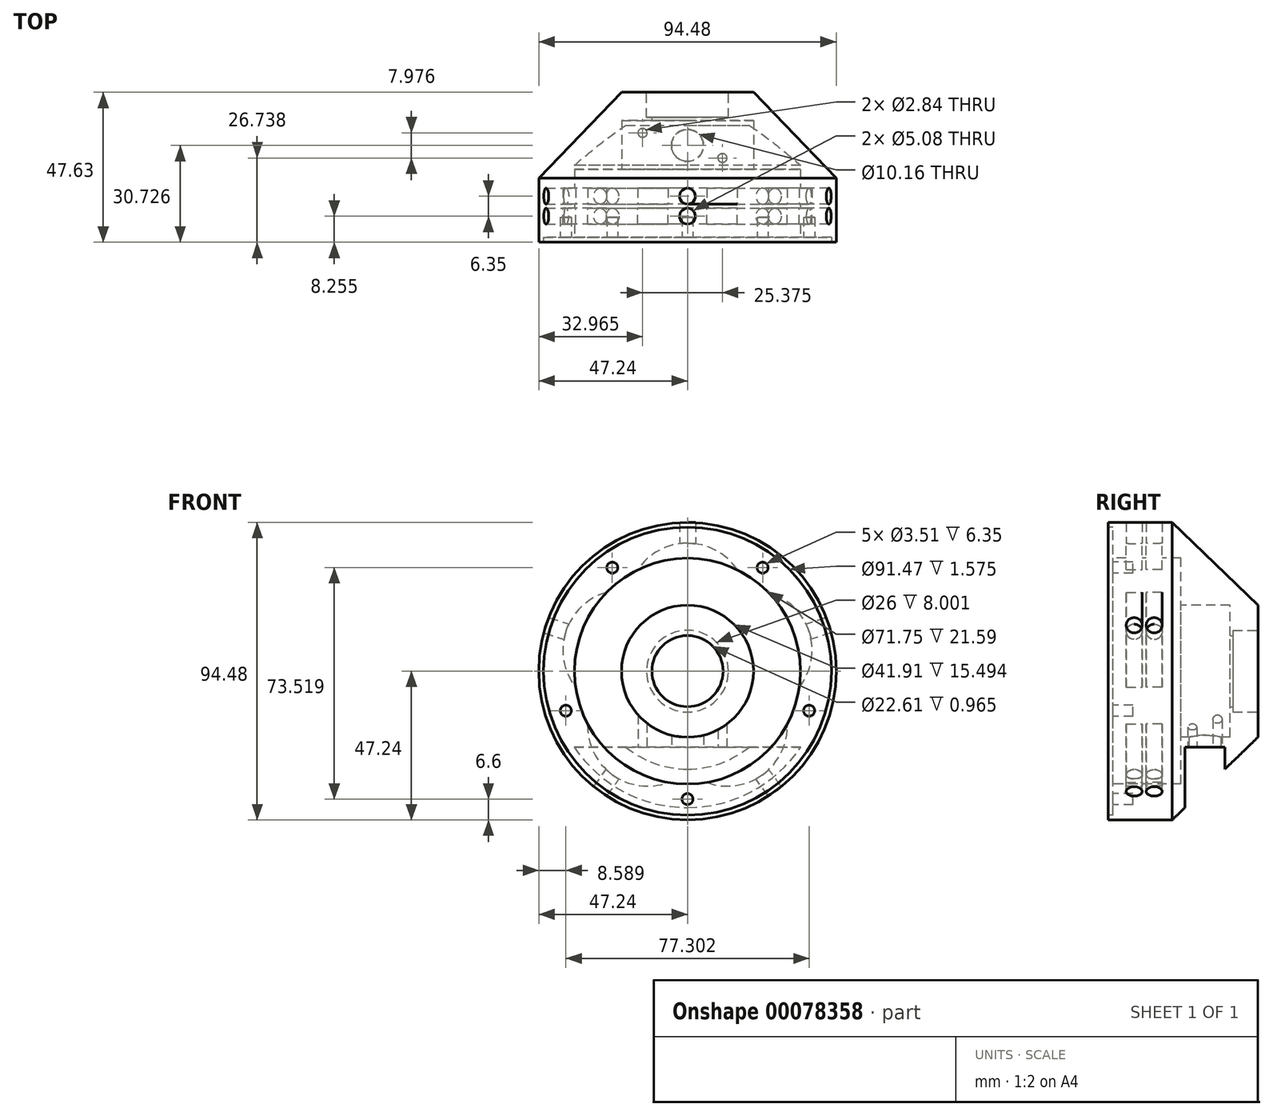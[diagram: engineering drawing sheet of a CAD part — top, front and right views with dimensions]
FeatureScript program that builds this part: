
annotation { "Feature Type Name" : "Feature", "Feature Type Description" : "" }
export const myFeature = defineFeature(function(context is Context, id is Id, definition is map)
    precondition{}
    {
        {
            var Q0;
            Q0=qCreatedBy(makeId("Front.planeOp"),FACE);
            var sketch = newSketch(context, id + "F0", { "sketchPlane" : qUnion([Q0])});
            skCircle(sketch, "E0", {"center": v(0, 0) * mm, "radius": 47.24 * mm});
            skSolve(sketch);
        }
        {
            var Q0;
            Q0 = qSketchRegion(id + "F0", true);
            extrude(context, id + "F1", {"entities" : qUnion([Q0]), "depth" : 20.32 * mm});
        }
        {
            var Q0;
            Q0=makeQuery(id+"F1.opExtrude","CAP_FACE",FACE,{"disambiguationData":[OSD([sQuery(id+"F0.wireOp",EDGE,"E0")])],"isStart":false});
            var sketch = newSketch(context, id + "F2", { "sketchPlane" : qUnion([Q0])});
            skCircle(sketch, "E1", {"center": v(0, 0) * mm, "radius": 45.73 * mm});
            skSolve(sketch);
        }
        {
            var Q0;
            Q0 = qSketchRegion(id + "F2", true);
            extrude(context, id + "F3", {"entities" : qUnion([Q0]), "operationType" : NewBodyOperationType.REMOVE, "oppositeDirection" : true, "depth" : 1.57 * mm});
        }
        {
            var Q0;
            Q0=qCreatedBy(makeId("Right.planeOp"),FACE);
            var sketch = newSketch(context, id + "F4", { "sketchPlane" : qUnion([Q0])});
            skLineSegment(sketch, "E2", {"start": v(0, 0) * mm, "end": v(27.3, 0) * mm});
            skLineSegment(sketch, "E3", {"start": v(27.3, 0) * mm, "end": v(27.3, 20.96) * mm});
            skLineSegment(sketch, "E4", {"start": v(0, 0) * mm, "end": v(0, 47.24) * mm});
            skLineSegment(sketch, "E5", {"start": v(0, 47.24) * mm, "end": v(27.3, 20.96) * mm});
            skSolve(sketch);
        }
        {
            var Q0;
            Q0 = qSketchRegion(id + "F4", true);
            var Q1;
            Q1=sQuery(id+"F4.wireOp",EDGE,"E2");
            revolve(context, id + "F5", {"operationType" : NewBodyOperationType.ADD, "entities" : qUnion([Q0]), "axis" : qUnion([Q1]), "revolveType" : RevolveType.FULL});
        }
        {
            var Q0;
            Q0=makeQuery(id+"F5.opRevolve","SWEPT_FACE",FACE,{"disambiguationData":[OSD([sQuery(id+"F4.wireOp",EDGE,"E3")])]});
            var sketch = newSketch(context, id + "F6", { "sketchPlane" : qUnion([Q0])});
            skCircle(sketch, "E6", {"center": v(0, 0) * mm, "radius": 13 * mm});
            skSolve(sketch);
        }
        {
            var Q0;
            Q0 = qSketchRegion(id + "F6", true);
            extrude(context, id + "F7", {"entities" : qUnion([Q0]), "operationType" : NewBodyOperationType.REMOVE, "oppositeDirection" : true, "depth" : 8 * mm});
        }
        {
            var Q0;
            Q0=makeQuery(id+"F3.boolean.opBoolean","COPY",FACE,{"derivedFrom":makeQuery(id+"F3.opExtrude","CAP_FACE",FACE,{"disambiguationData":[OSD([sQuery(id+"F2.wireOp",EDGE,"E1")])],"isStart":false})});
            var sketch = newSketch(context, id + "F8", { "sketchPlane" : qUnion([Q0])});
            skCircle(sketch, "E7", {"center": v(0, 0) * mm, "radius": 35.88 * mm});
            skSolve(sketch);
        }
        {
            var Q0;
            Q0 = qSketchRegion(id + "F8", true);
            extrude(context, id + "F9", {"entities" : qUnion([Q0]), "operationType" : NewBodyOperationType.REMOVE, "oppositeDirection" : true, "depth" : 21.59 * mm});
        }
        {
            var Q0;
            Q0=makeQuery(id+"F9.boolean.opBoolean","COPY",FACE,{"derivedFrom":makeQuery(id+"F9.opExtrude","CAP_FACE",FACE,{"disambiguationData":[OSD([sQuery(id+"F8.wireOp",EDGE,"E7")])],"isStart":false})});
            var sketch = newSketch(context, id + "F10", { "sketchPlane" : qUnion([Q0])});
            skCircle(sketch, "E8", {"center": v(0, 0) * mm, "radius": 20.96 * mm});
            skSolve(sketch);
        }
        {
            var Q0;
            Q0 = qSketchRegion(id + "F10", true);
            extrude(context, id + "F11", {"entities" : qUnion([Q0]), "operationType" : NewBodyOperationType.REMOVE, "oppositeDirection" : true, "depth" : 15.5 * mm});
        }
        {
            var Q0;
            Q0=makeQuery(id+"F7.boolean.opBoolean","COPY",FACE,{"derivedFrom":makeQuery(id+"F7.opExtrude","CAP_FACE",FACE,{"disambiguationData":[OSD([sQuery(id+"F6.wireOp",EDGE,"E6")])],"isStart":false})});
            var sketch = newSketch(context, id + "F12", { "sketchPlane" : qUnion([Q0])});
            skCircle(sketch, "E9", {"center": v(0, 0) * mm, "radius": 11.3 * mm});
            skSolve(sketch);
        }
        {
            var Q0;
            Q0 = qSketchRegion(id + "F12", true);
            extrude(context, id + "F13", {"entities" : qUnion([Q0]), "operationType" : NewBodyOperationType.REMOVE, "oppositeDirection" : true, "depth" : 25.4 * mm});
        }
        {
            var Q0;
            Q0=qCreatedBy(makeId("Top.planeOp"),FACE);
            cPlane(context, id + "F14", {"entities" : qUnion([Q0]), "cplaneType" : CPlaneType.OFFSET, "offset" : 24.13 * mm, "oppositeDirection" : true, "width" : 152.4 * mm, "height" : 152.4 * mm});
        }
        {
            var Q0;
            Q0=qCreatedBy(id+"F14.planeOp",FACE);
            var sketch = newSketch(context, id + "F15", { "sketchPlane" : qUnion([Q0])});
            skLineSegment(sketch, "E10", {"start": v(0, 16.76) * mm, "end": v(-59.54, 16.76) * mm});
            skLineSegment(sketch, "E11", {"start": v(0, 4.06) * mm, "end": v(-59.54, 4.06) * mm});
            skLineSegment(sketch, "E12", {"start": v(-59.54, 4.06) * mm, "end": v(-59.54, 16.76) * mm});
            skLineSegment(sketch, "E13.MirrorCS", {"start": v(0, 4.06) * mm, "end": v(59.54, 4.06) * mm});
            skLineSegment(sketch, "E14.MirrorCS", {"start": v(0, 16.76) * mm, "end": v(59.54, 16.76) * mm});
            skLineSegment(sketch, "E15.MirrorCS", {"start": v(59.54, 4.06) * mm, "end": v(59.54, 16.76) * mm});
            skSolve(sketch);
        }
        {
            var Q0;
            Q0 = qSketchRegion(id + "F15", true);
            extrude(context, id + "F16", {"entities" : qUnion([Q0]), "operationType" : NewBodyOperationType.REMOVE, "oppositeDirection" : true, "depth" : 25.4 * mm});
        }
        {
            var Q0;
            Q0=makeQuery(id+"F16.boolean.opBoolean","COPY",FACE,{"derivedFrom":makeQuery(id+"F16.opExtrude","CAP_FACE",FACE,{"disambiguationData":[OSD([sQuery(id+"F15.wireOp",EDGE,"E10"),sQuery(id+"F15.wireOp",EDGE,"E11"),sQuery(id+"F15.wireOp",EDGE,"E12"),sQuery(id+"F15.wireOp",EDGE,"E13.MirrorCS"),sQuery(id+"F15.wireOp",EDGE,"E14.MirrorCS"),sQuery(id+"F15.wireOp",EDGE,"E15.MirrorCS")])],"isStart":true})});
            var sketch = newSketch(context, id + "F17", { "sketchPlane" : qUnion([Q0])});
            skPoint(sketch, "E16.endSnap0", {"position": v(0, -16.76) * mm});
            skCircle(sketch, "E17", {"center": v(0, -10.4) * mm, "radius": 5.08 * mm});
            skLineSegment(sketch, "E18", {"start": v(0, -10.4) * mm, "end": v(11.1, -10.4) * mm, "construction": true});
            skLineSegment(sketch, "E19", {"start": v(0, -10.4) * mm, "end": v(-14.27, -10.4) * mm, "construction": true});
            skLineSegment(sketch, "E20", {"start": v(11.1, -10.4) * mm, "end": v(11.1, -6.42) * mm, "construction": true});
            skLineSegment(sketch, "E21", {"start": v(-14.27, -10.4) * mm, "end": v(-14.27, -14.4) * mm, "construction": true});
            skCircle(sketch, "E22", {"center": v(11.1, -6.42) * mm, "radius": 1.42 * mm});
            skCircle(sketch, "E23", {"center": v(-14.27, -14.4) * mm, "radius": 1.42 * mm});
            skSolve(sketch);
        }
        {
            var Q0;
            Q0 = qSketchRegion(id + "F17", true);
            extrude(context, id + "F18", {"entities" : qUnion([Q0]), "operationType" : NewBodyOperationType.REMOVE, "oppositeDirection" : true, "depth" : 25.4 * mm});
        }
        {
            var Q0;
            Q0=makeQuery(id+"F3.boolean.opBoolean","COPY",FACE,{"derivedFrom":makeQuery(id+"F3.opExtrude","CAP_FACE",FACE,{"disambiguationData":[OSD([sQuery(id+"F2.wireOp",EDGE,"E1")])],"isStart":false})});
            var sketch = newSketch(context, id + "F19", { "sketchPlane" : qUnion([Q0])});
            skCircle(sketch, "E24", {"center": v(0, -40.64) * mm, "radius": 1.75 * mm});
            skCircle(sketch, "E25.1.0", {"center": v(-38.65, -12.56) * mm, "radius": 1.75 * mm});
            skCircle(sketch, "E25.2.0", {"center": v(-23.89, 32.88) * mm, "radius": 1.75 * mm});
            skCircle(sketch, "E25.3.0", {"center": v(23.89, 32.88) * mm, "radius": 1.75 * mm});
            skCircle(sketch, "E25.4.0", {"center": v(38.65, -12.56) * mm, "radius": 1.75 * mm});
            skPoint(sketch, "E25.center", {"position": v(0, 0) * mm});
            skSolve(sketch);
        }
        {
            var Q0;
            Q0 = qSketchRegion(id + "F19", true);
            extrude(context, id + "F20", {"entities" : qUnion([Q0]), "operationType" : NewBodyOperationType.REMOVE, "oppositeDirection" : true, "depth" : 6.35 * mm});
        }
        {
            var Q0;
            Q0=makeQuery(id+"F1.opExtrude","CAP_FACE",FACE,{"disambiguationData":[OSD([sQuery(id+"F0.wireOp",EDGE,"E0")])],"isStart":false});
            cPlane(context, id + "F21", {"entities" : qUnion([Q0]), "cplaneType" : CPlaneType.OFFSET, "offset" : 8.25 * mm, "oppositeDirection" : true, "width" : 152.4 * mm, "height" : 152.4 * mm});
        }
        {
            var Q0;
            Q0=makeQuery(id+"F1.opExtrude","CAP_FACE",FACE,{"disambiguationData":[OSD([sQuery(id+"F0.wireOp",EDGE,"E0")])],"isStart":false});
            cPlane(context, id + "F22", {"entities" : qUnion([Q0]), "cplaneType" : CPlaneType.OFFSET, "offset" : 14.6 * mm, "oppositeDirection" : true, "width" : 152.4 * mm, "height" : 152.4 * mm});
        }
        {
            var Q0;
            Q0=qCreatedBy(id+"F21.planeOp",FACE);
            var sketch = newSketch(context, id + "F23", { "sketchPlane" : qUnion([Q0])});
            skPoint(sketch, "E26", {"position": v(0, 40.64) * mm});
            skPoint(sketch, "E27.2.0", {"position": v(-38.65, 12.56) * mm});
            skPoint(sketch, "E27.4.0", {"position": v(-23.89, -32.88) * mm});
            skPoint(sketch, "E27.6.0", {"position": v(23.89, -32.88) * mm});
            skPoint(sketch, "E27.8.0", {"position": v(38.65, 12.56) * mm});
            skPoint(sketch, "E27.center", {"position": v(0, 0) * mm});
            skArc(sketch, "E28", {"start": v(15.82, 32.2) * mm, "mid": v(0, 40.64) * mm, "end": v(-15.82, 32.2) * mm});
            skArc(sketch, "E29", {"start": v(15.82, 32.2) * mm, "mid": v(0, 35.88) * mm, "end": v(-15.82, 32.2) * mm});
            skArc(sketch, "E30.1.0", {"start": v(-25.74, 25) * mm, "mid": v(-34.12, 11.09) * mm, "end": v(-35.51, -5.1) * mm});
            skArc(sketch, "E30.1.1", {"start": v(-25.74, 25) * mm, "mid": v(-38.65, 12.56) * mm, "end": v(-35.51, -5.1) * mm});
            skArc(sketch, "E30.2.0", {"start": v(-31.73, -16.75) * mm, "mid": v(-21.09, -29.03) * mm, "end": v(-6.13, -35.35) * mm});
            skArc(sketch, "E30.2.1", {"start": v(-31.73, -16.75) * mm, "mid": v(-23.89, -32.88) * mm, "end": v(-6.13, -35.35) * mm});
            skArc(sketch, "E30.3.0", {"start": v(6.13, -35.35) * mm, "mid": v(21.09, -29.03) * mm, "end": v(31.73, -16.75) * mm});
            skArc(sketch, "E30.3.1", {"start": v(6.13, -35.35) * mm, "mid": v(23.89, -32.88) * mm, "end": v(31.73, -16.75) * mm});
            skArc(sketch, "E30.4.0", {"start": v(35.51, -5.1) * mm, "mid": v(34.12, 11.09) * mm, "end": v(25.74, 25) * mm});
            skArc(sketch, "E30.4.1", {"start": v(35.51, -5.1) * mm, "mid": v(38.65, 12.56) * mm, "end": v(25.74, 25) * mm});
            skSolve(sketch);
        }
        {
            var Q0;
            Q0 = qSketchRegion(id + "F23", true);
            extrude(context, id + "F24", {"entities" : qUnion([Q0]), "operationType" : NewBodyOperationType.REMOVE, "endBound" : BoundingType.SYMMETRIC, "depth" : 5.08 * mm});
        }
        {
            var Q0;
            Q0=qCreatedBy(id+"F22.planeOp",FACE);
            var sketch = newSketch(context, id + "F25", { "sketchPlane" : qUnion([Q0])});
            skArc(sketch, "E31", {"start": v(15.82, 32.2) * mm, "mid": v(0, 35.88) * mm, "end": v(-15.82, 32.2) * mm});
            skArc(sketch, "E32", {"start": v(15.82, 32.2) * mm, "mid": v(0, 40.64) * mm, "end": v(-15.82, 32.2) * mm});
            skArc(sketch, "E33.1.0", {"start": v(-25.74, 25) * mm, "mid": v(-38.65, 12.56) * mm, "end": v(-35.51, -5.1) * mm});
            skArc(sketch, "E33.1.1", {"start": v(-25.74, 25) * mm, "mid": v(-34.12, 11.09) * mm, "end": v(-35.51, -5.1) * mm});
            skArc(sketch, "E33.2.0", {"start": v(-31.73, -16.75) * mm, "mid": v(-23.89, -32.88) * mm, "end": v(-6.13, -35.35) * mm});
            skArc(sketch, "E33.2.1", {"start": v(-31.73, -16.75) * mm, "mid": v(-21.09, -29.03) * mm, "end": v(-6.13, -35.35) * mm});
            skArc(sketch, "E33.3.0", {"start": v(6.13, -35.35) * mm, "mid": v(23.89, -32.88) * mm, "end": v(31.73, -16.75) * mm});
            skArc(sketch, "E33.3.1", {"start": v(6.13, -35.35) * mm, "mid": v(21.09, -29.03) * mm, "end": v(31.73, -16.75) * mm});
            skArc(sketch, "E33.4.0", {"start": v(35.51, -5.1) * mm, "mid": v(38.65, 12.56) * mm, "end": v(25.74, 25) * mm});
            skArc(sketch, "E33.4.1", {"start": v(35.51, -5.1) * mm, "mid": v(34.12, 11.09) * mm, "end": v(25.74, 25) * mm});
            skSolve(sketch);
        }
        {
            var Q0;
            Q0 = qSketchRegion(id + "F25", true);
            extrude(context, id + "F26", {"entities" : qUnion([Q0]), "operationType" : NewBodyOperationType.REMOVE, "endBound" : BoundingType.SYMMETRIC, "oppositeDirection" : true, "depth" : 5.08 * mm});
        }
        {
            var Q0;
            Q0=qCreatedBy(makeId("Top.planeOp"),FACE);
            var sketch = newSketch(context, id + "F27", { "sketchPlane" : qUnion([Q0])});
            skCircle(sketch, "E34", {"center": v(0, -5.72) * mm, "radius": 2.54 * mm});
            skCircle(sketch, "E35", {"center": v(0, -12.07) * mm, "radius": 2.54 * mm});
            skSolve(sketch);
        }
        {
            var Q0;
            Q0 = qSketchRegion(id + "F27", true);
            extrude(context, id + "F28", {"entities" : qUnion([Q0]), "depth" : 50.8 * mm});
        }
        {
            var Q0;
            Q0=makeQuery(id+"F28.opExtrude","SWEPT_BODY",BODY,{"disambiguationData":[OSD([sQuery(id+"F27.wireOp",EDGE,"E35")])]});
            var Q1;
            Q1=makeQuery(id+"F28.opExtrude","SWEPT_BODY",BODY,{"disambiguationData":[OSD([sQuery(id+"F27.wireOp",EDGE,"E34")])]});
            var Q2;
            Q2=makeQuery(id+"F9.boolean.opBoolean","COPY",FACE,{"derivedFrom":makeQuery(id+"F9.opExtrude","SWEPT_FACE",FACE,{"disambiguationData":[OSD([sQuery(id+"F8.wireOp",EDGE,"E7")])]})});
            circularPattern(context, id + "F29", {"operationType" : NewBodyOperationType.REMOVE, "entities" : qUnion([Q0, Q1]), "axis" : qUnion([Q2]), "angle" : 72 * degree, "instanceCount" : 5});
        }
    });
